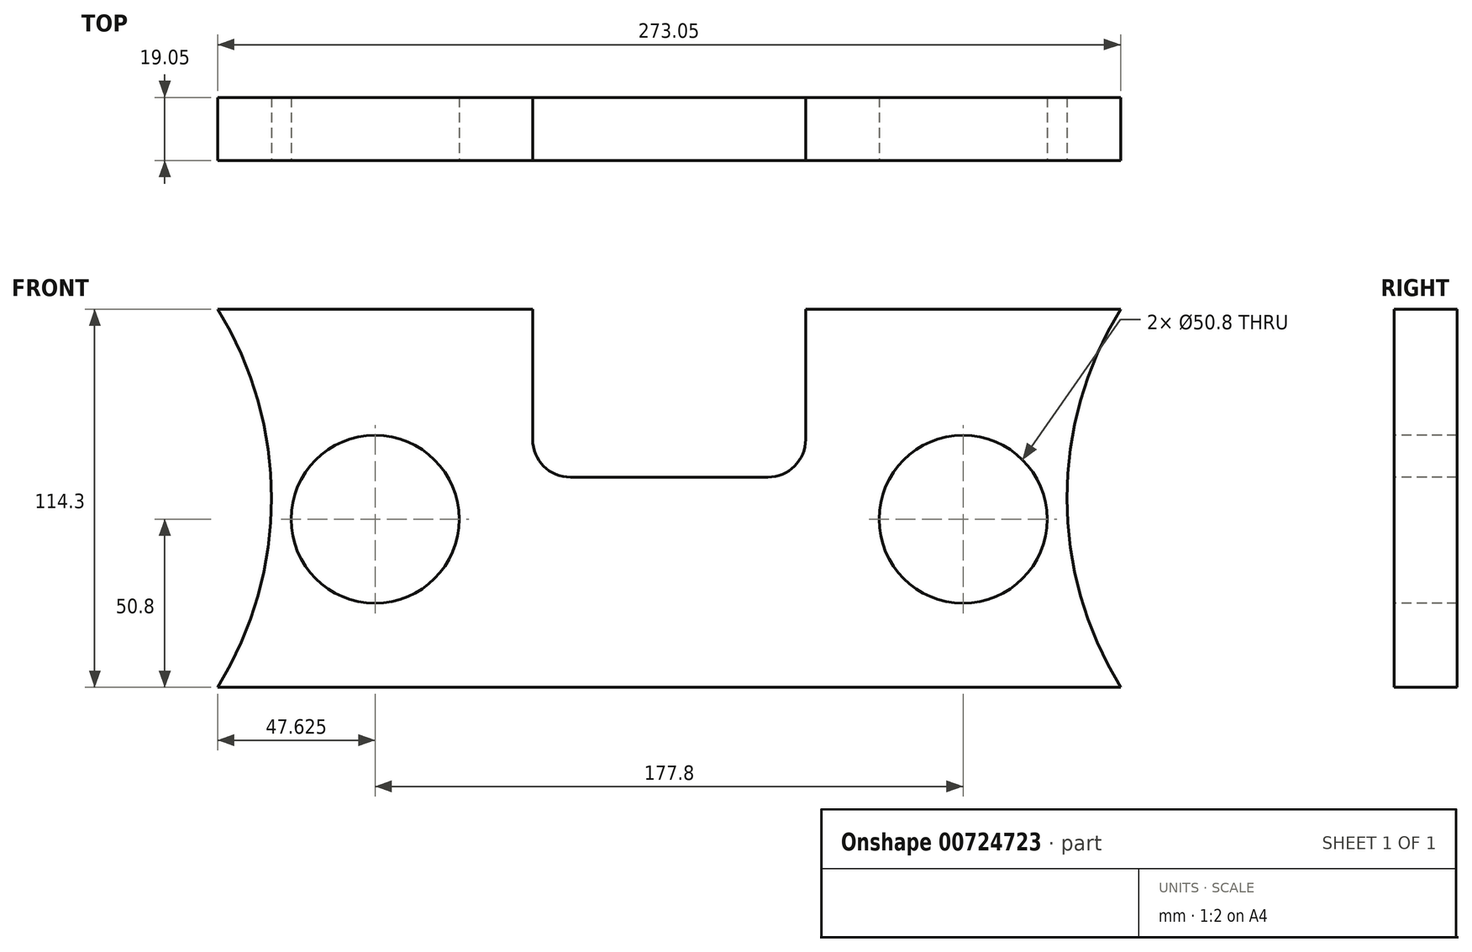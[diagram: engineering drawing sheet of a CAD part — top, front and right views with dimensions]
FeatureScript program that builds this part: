
annotation { "Feature Type Name" : "Feature", "Feature Type Description" : "" }
export const myFeature = defineFeature(function(context is Context, id is Id, definition is map)
    precondition{}
    {
        {
            var Q0;
            Q0=qCreatedBy(makeId("Front.planeOp"),FACE);
            var sketch = newSketch(context, id + "F0", { "sketchPlane" : qUnion([Q0])});
            skLineSegment(sketch, "E0.bottom", {"start": v(0, 0) * mm, "end": v(273.05, 0) * mm});
            skLineSegment(sketch, "E0.top", {"start": v(0, 114.3) * mm, "end": v(273.05, 114.3) * mm});
            skLineSegment(sketch, "E0.left", {"start": v(0, 0) * mm, "end": v(0, 114.3) * mm});
            skLineSegment(sketch, "E0.right", {"start": v(273.05, 0) * mm, "end": v(273.05, 114.3) * mm});
            skSolve(sketch);
        }
        {
            var Q0;
            Q0=qSketchRegion(id+"F0",true);
            extrude(context, id + "F1", {"entities" : qUnion([Q0]), "depth" : 19.05 * mm, "offsetDistance" : 25.4 * mm});
        }
        {
            var Q0;
            Q0=makeQuery(id+"F1.opExtrude","CAP_FACE",FACE,{"disambiguationData":[OSD([sQuery(id+"F0.wireOp",EDGE,"E0.bottom"),sQuery(id+"F0.wireOp",EDGE,"E0.top"),sQuery(id+"F0.wireOp",EDGE,"E0.left"),sQuery(id+"F0.wireOp",EDGE,"E0.right")])],"isStart":false});
            var sketch = newSketch(context, id + "F2", { "sketchPlane" : qUnion([Q0])});
            skCircle(sketch, "E1", {"center": v(47.63, 50.8) * mm, "radius": 25.4 * mm});
            skCircle(sketch, "E2", {"center": v(225.43, 50.8) * mm, "radius": 25.4 * mm});
            skArc(sketch, "E3", {"start": v(0, 0) * mm, "mid": v(12.7, 57.15) * mm, "end": v(0, 114.3) * mm});
            skArc(sketch, "E4", {"start": v(273.05, 114.3) * mm, "mid": v(260.35, 57.15) * mm, "end": v(273.05, 0) * mm});
            skSolve(sketch);
        }
        {
            var Q0;
            Q0=qSketchRegion(id+"F2",true);
            extrude(context, id + "F3", {"entities" : qUnion([Q0]), "operationType" : NewBodyOperationType.REMOVE, "oppositeDirection" : true, "depth" : 25.4 * mm, "offsetDistance" : 25.4 * mm});
        }
        {
            var Q0;
            Q0=makeQuery(id+"F1.opExtrude","CAP_FACE",FACE,{"disambiguationData":[OSD([sQuery(id+"F0.wireOp",EDGE,"E0.bottom"),sQuery(id+"F0.wireOp",EDGE,"E0.top"),sQuery(id+"F0.wireOp",EDGE,"E0.left"),sQuery(id+"F0.wireOp",EDGE,"E0.right")])],"isStart":false});
            var sketch = newSketch(context, id + "F4", { "sketchPlane" : qUnion([Q0])});
            skLineSegment(sketch, "E5", {"start": v(95.25, 114.3) * mm, "end": v(95.25, 74.93) * mm});
            skLineSegment(sketch, "E6", {"start": v(106.68, 63.5) * mm, "end": v(166.37, 63.5) * mm});
            skLineSegment(sketch, "E7", {"start": v(177.8, 74.93) * mm, "end": v(177.8, 114.3) * mm});
            skPoint(sketch, "E8.visualSharp", {"position": v(95.25, 63.5) * mm});
            skArc(sketch, "E8.filletArc", {"start": v(95.25, 74.93) * mm, "mid": v(98.6, 66.85) * mm, "end": v(106.68, 63.5) * mm});
            skPoint(sketch, "E9.visualSharp", {"position": v(177.8, 63.5) * mm});
            skArc(sketch, "E9.filletArc", {"start": v(166.37, 63.5) * mm, "mid": v(174.45, 66.85) * mm, "end": v(177.8, 74.93) * mm});
            skSolve(sketch);
        }
        {
            var Q0;
            Q0=qSketchRegion(id+"F4",true);
            var Q1;
            {var subQ1=sQuery(id+"F4.wireOp",EDGE,"E5");Q1=makeQuery(id+"F4.imprint","IMPRINT",FACE,{"disambiguationData":[TD([[makeQuery(id+"F4.imprint","IMPRINT",EDGE,{"derivedFrom":subQ1}),1.0]])]});}
            extrude(context, id + "F5", {"entities" : qUnion([Q0, Q1]), "operationType" : NewBodyOperationType.REMOVE, "oppositeDirection" : true, "depth" : 25.4 * mm, "offsetDistance" : 25.4 * mm});
        }
        {
            var Q0;
            Q0=makeQuery(id+"F1.opExtrude","CAP_FACE",FACE,{"disambiguationData":[OSD([sQuery(id+"F0.wireOp",EDGE,"E0.bottom"),sQuery(id+"F0.wireOp",EDGE,"E0.top"),sQuery(id+"F0.wireOp",EDGE,"E0.left"),sQuery(id+"F0.wireOp",EDGE,"E0.right")])],"isStart":false});
            var sketch = newSketch(context, id + "F6", { "sketchPlane" : qUnion([Q0])});
            skLineSegment(sketch, "E10", {"start": v(140.97, 38.1) * mm, "end": v(140.97, 25.4) * mm});
            skLineSegment(sketch, "E11", {"start": v(140.97, 25.4) * mm, "end": v(76.02, 25.4) * mm});
            skLineSegment(sketch, "E12", {"start": v(225.43, 12.7) * mm, "end": v(197.03, 25.4) * mm});
            skLineSegment(sketch, "E13", {"start": v(197.03, 25.4) * mm, "end": v(166.37, 25.4) * mm});
            skLineSegment(sketch, "E14", {"start": v(166.37, 25.4) * mm, "end": v(166.37, 38.1) * mm});
            skLineSegment(sketch, "E15", {"start": v(76.02, 25.4) * mm, "end": v(47.63, 12.7) * mm});
            skLineSegment(sketch, "E16", {"start": v(47.63, 12.7) * mm, "end": v(225.43, 12.7) * mm});
            skArc(sketch, "E17", {"start": v(0, 0) * mm, "mid": v(16.27, 57.15) * mm, "end": v(0, 114.3) * mm});
            skArc(sketch, "E18", {"start": v(273.05, 114.3) * mm, "mid": v(256.78, 57.15) * mm, "end": v(273.05, 0) * mm});
            skSolve(sketch);
        }
        {
            var Q0;
            Q0 = qSketchRegion(id + "F6", true);
            var Q1;
            Q1=makeQuery(id+"F6.imprint","IMPRINT",FACE,{"disambiguationData":[TD([[makeQuery(id+"F6.imprint","IMPRINT",EDGE,{"derivedFrom":sQuery(id+"F6.wireOp",EDGE,"E17")}),1.0]])]});
            var Q2;
            Q2=makeQuery(id+"F6.imprint","IMPRINT",FACE,{"disambiguationData":[TD([[makeQuery(id+"F6.imprint","IMPRINT",EDGE,{"derivedFrom":sQuery(id+"F6.wireOp",EDGE,"E18")}),1.0]])]});
            extrude(context, id + "F7", {"entities" : qUnion([Q0, Q1, Q2]), "operationType" : NewBodyOperationType.REMOVE, "oppositeDirection" : true, "depth" : 25.4 * mm, "offsetDistance" : 25.4 * mm});
        }
    });
